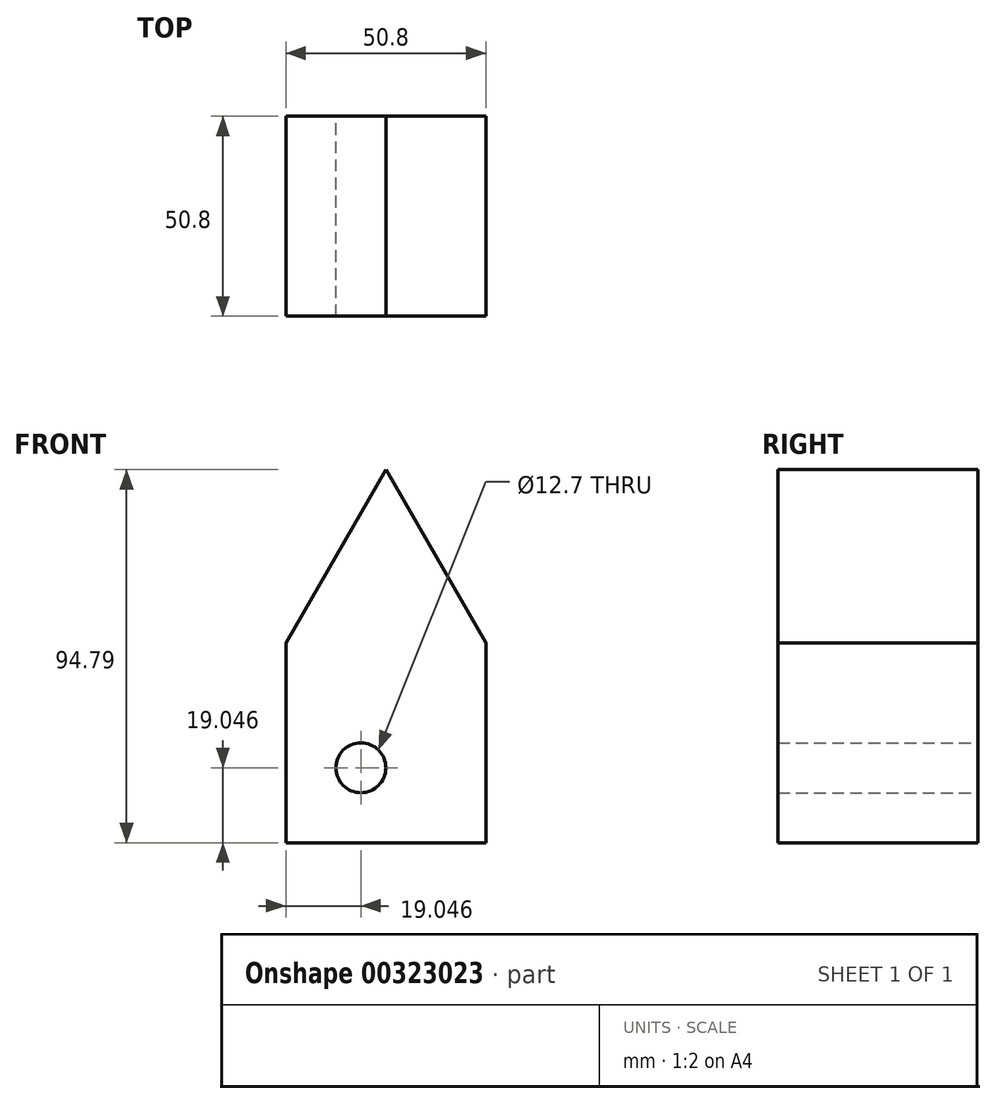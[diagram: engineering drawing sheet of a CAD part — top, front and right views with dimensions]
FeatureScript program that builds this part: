
annotation { "Feature Type Name" : "Feature", "Feature Type Description" : "" }
export const myFeature = defineFeature(function(context is Context, id is Id, definition is map)
    precondition{}
    {
        {
            var Q0;
            Q0=qCreatedBy(makeId("Front.planeOp"),FACE);
            var sketch = newSketch(context, id + "F0", { "sketchPlane" : qUnion([Q0])});
            skLineSegment(sketch, "E0.top", {"start": v(-21.23, -31.55) * mm, "end": v(29.57, -31.55) * mm});
            skLineSegment(sketch, "E0.left", {"start": v(-21.23, 19.25) * mm, "end": v(-21.23, -31.55) * mm});
            skLineSegment(sketch, "E0.right", {"start": v(29.57, 19.25) * mm, "end": v(29.57, -31.55) * mm});
            skLineSegment(sketch, "E1", {"start": v(-21.23, 19.25) * mm, "end": v(4.17, 63.24) * mm});
            skLineSegment(sketch, "E2", {"start": v(4.17, 63.24) * mm, "end": v(29.57, 19.25) * mm});
            skCircle(sketch, "E3", {"center": v(-2.18, -12.5) * mm, "radius": 6.35 * mm});
            skSolve(sketch);
        }
        {
            var Q0;
            Q0 = qSketchRegion(id + "F0", true);
            extrude(context, id + "F1", {"entities" : qUnion([Q0]), "depth" : 50.8 * mm});
        }
    });
